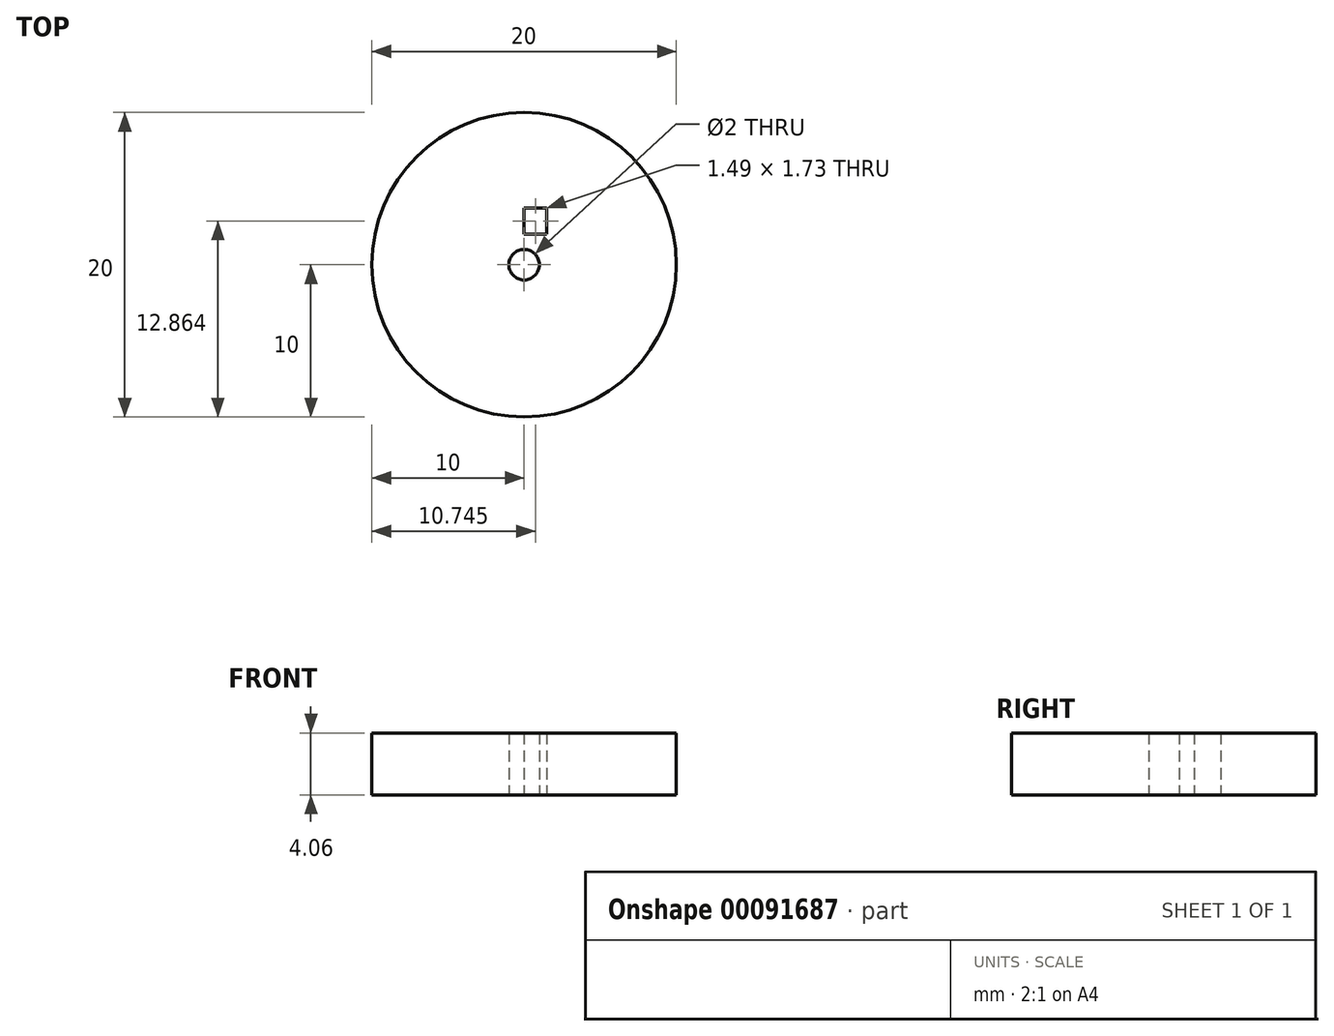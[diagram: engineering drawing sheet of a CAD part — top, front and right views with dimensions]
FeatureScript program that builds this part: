
annotation { "Feature Type Name" : "Feature", "Feature Type Description" : "" }
export const myFeature = defineFeature(function(context is Context, id is Id, definition is map)
    precondition{}
    {
        {
            var Q0;
            Q0=qCreatedBy(makeId("Top.planeOp"),FACE);
            var sketch = newSketch(context, id + "F0", { "sketchPlane" : qUnion([Q0])});
            skCircle(sketch, "E0", {"center": v(0, 0) * mm, "radius": 10 * mm});
            skCircle(sketch, "E1", {"center": v(0, 0) * mm, "radius": 1 * mm});
            skLineSegment(sketch, "E2.bottom", {"start": v(0, 3.73) * mm, "end": v(1.5, 3.73) * mm});
            skLineSegment(sketch, "E2.top", {"start": v(0, 2) * mm, "end": v(1.5, 2) * mm});
            skLineSegment(sketch, "E2.left", {"start": v(0, 3.73) * mm, "end": v(0, 2) * mm});
            skLineSegment(sketch, "E2.right", {"start": v(1.5, 3.73) * mm, "end": v(1.5, 2) * mm});
            skSolve(sketch);
        }
        {
            var Q0;
            Q0=makeQuery(id+"F0.imprint","IMPRINT",FACE,{"disambiguationData":[TD([[makeQuery(id+"F0.imprint","IMPRINT",EDGE,{"derivedFrom":sQuery(id+"F0.wireOp",EDGE,"E0")}),1.0]])]});
            extrude(context, id + "F1", {"entities" : qUnion([Q0]), "depth" : 4.06 * mm});
        }
    });
